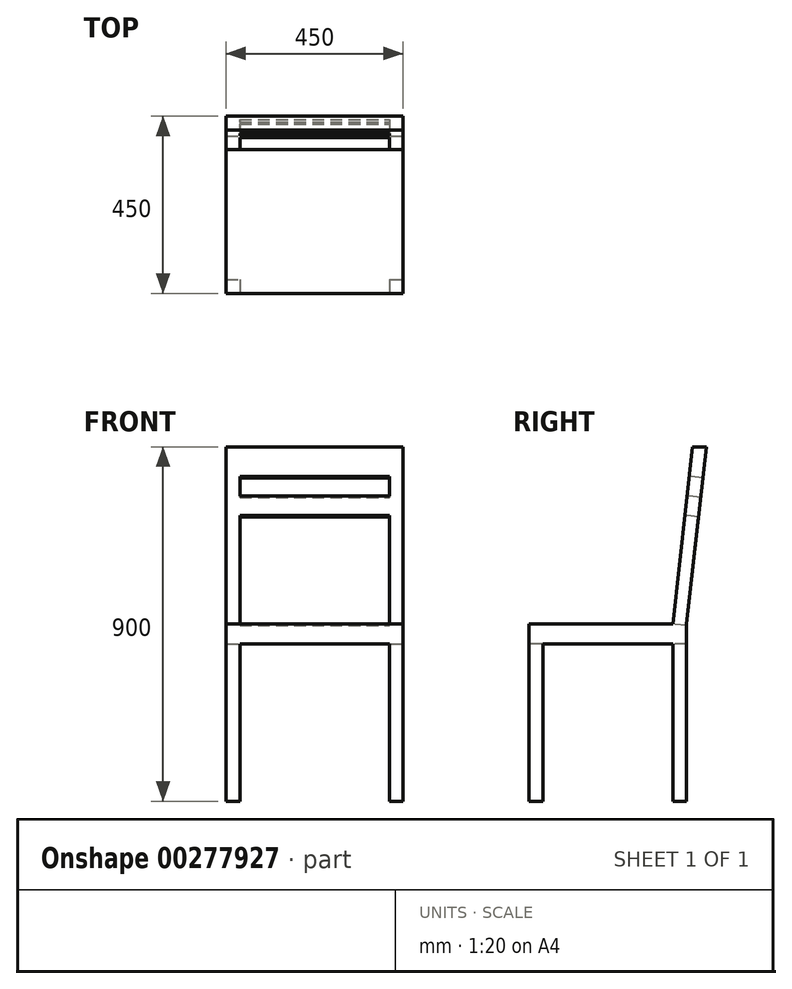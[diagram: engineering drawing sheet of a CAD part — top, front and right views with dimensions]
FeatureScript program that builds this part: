
annotation { "Feature Type Name" : "Feature", "Feature Type Description" : "" }
export const myFeature = defineFeature(function(context is Context, id is Id, definition is map)
    precondition{}
    {
        {
            var Q0;
            Q0=qCreatedBy(makeId("Front.planeOp"),FACE);
            var sketch = newSketch(context, id + "F0", { "sketchPlane" : qUnion([Q0])});
            skLineSegment(sketch, "E0.bottom", {"start": v(-225, 0) * mm, "end": v(225, 0) * mm});
            skLineSegment(sketch, "E0.top", {"start": v(-225, 900) * mm, "end": v(225, 900) * mm});
            skLineSegment(sketch, "E0.left", {"start": v(-225, 0) * mm, "end": v(-225, 900) * mm});
            skLineSegment(sketch, "E0.right", {"start": v(225, 0) * mm, "end": v(225, 900) * mm});
            skSolve(sketch);
        }
        {
            var Q0;
            Q0 = qSketchRegion(id + "F0", true);
            var Q1;
            Q1 = qSketchRegion(id + "F2", true);
            extrude(context, id + "F1", {"entities" : qUnion([Q0, Q1]), "depth" : 450 * mm, "symmetric" : true});
        }
        {
            var Q0;
            Q0=makeQuery(id+"F1.opExtrude","SWEPT_FACE",FACE,{"disambiguationData":[OSD([sQuery(id+"F0.wireOp",EDGE,"E0.right")])]});
            var sketch = newSketch(context, id + "F2", { "sketchPlane" : qUnion([Q0])});
            skLineSegment(sketch, "E1.bottom", {"start": v(225, 450) * mm, "end": v(-225, 450) * mm});
            skLineSegment(sketch, "E1.top", {"start": v(225, 400) * mm, "end": v(-225, 400) * mm});
            skLineSegment(sketch, "E1.left", {"start": v(225, 450) * mm, "end": v(225, 400) * mm});
            skLineSegment(sketch, "E1.right", {"start": v(-225, 450) * mm, "end": v(-225, 400) * mm});
            skLineSegment(sketch, "E2", {"start": v(225, 900) * mm, "end": v(175, 450) * mm});
            skLineSegment(sketch, "E3", {"start": v(190, 900) * mm, "end": v(140, 450) * mm});
            skLineSegment(sketch, "E4", {"start": v(175, 450) * mm, "end": v(175, 0) * mm});
            skLineSegment(sketch, "E5", {"start": v(140, 450) * mm, "end": v(140, 0) * mm});
            skLineSegment(sketch, "E6.bottom", {"start": v(-225, 400) * mm, "end": v(-190, 400) * mm});
            skLineSegment(sketch, "E6.top", {"start": v(-225, 0) * mm, "end": v(-190, 0) * mm});
            skLineSegment(sketch, "E6.left", {"start": v(-225, 400) * mm, "end": v(-225, 0) * mm});
            skLineSegment(sketch, "E6.right", {"start": v(-190, 400) * mm, "end": v(-190, 0) * mm});
            skSolve(sketch);
        }
        {
            var Q0;
            {var subQ4=sQuery(id+"F2.wireOp",EDGE,"E3");Q0=makeQuery(id+"F2.imprint","IMPRINT",FACE,{"disambiguationData":[TD([[makeQuery(id+"F2.imprint","IMPRINT",EDGE,{"derivedFrom":subQ4}),-1.0]])]});}
            var Q1;
            {var subQ4=sQuery(id+"F2.wireOp",EDGE,"E2");Q1=makeQuery(id+"F2.imprint","IMPRINT",FACE,{"disambiguationData":[TD([[makeQuery(id+"F2.imprint","IMPRINT",EDGE,{"derivedFrom":subQ4}),1.0]])]});}
            var Q2;
            {var subQ0=sQuery(id+"F2.wireOp",EDGE,"E1.left");Q2=makeQuery(id+"F2.imprint","IMPRINT",FACE,{"disambiguationData":[TD([[makeQuery(id+"F2.imprint","IMPRINT",EDGE,{"derivedFrom":subQ0}),1.0]])]});}
            var Q3;
            {var subQ0=sQuery(id+"F2.wireOp",EDGE,"E1.top");var subQ4=sQuery(id+"F2.wireOp",EDGE,"E4");var subQ5=makeQuery(id+"F2.imprint","INTERSECT",VERTEX,{"derivedFrom":[subQ0,subQ4]});Q3=makeQuery(id+"F2.imprint","IMPRINT",FACE,{"disambiguationData":[TD([[makeQuery(id+"F2.imprint","IMPRINT",EDGE,{"disambiguationData":[TD([[subQ5,1.0]])],"derivedFrom":subQ0}),1.0]])]});}
            var Q4;
            {var subQ0=sQuery(id+"F2.wireOp",EDGE,"E6.right");Q4=makeQuery(id+"F2.imprint","IMPRINT",FACE,{"disambiguationData":[TD([[makeQuery(id+"F2.imprint","IMPRINT",EDGE,{"derivedFrom":subQ0}),1.0]])]});}
            extrude(context, id + "F3", {"entities" : qUnion([Q0, Q1, Q2, Q3, Q4]), "operationType" : NewBodyOperationType.REMOVE, "endBound" : BoundingType.THROUGH_ALL, "oppositeDirection" : true, "depth" : 25 * mm});
        }
        {
            var Q0;
            Q0=makeQuery(id+"F1.opExtrude","CAP_FACE",FACE,{"disambiguationData":[OSD([sQuery(id+"F0.wireOp",EDGE,"E0.bottom"),sQuery(id+"F0.wireOp",EDGE,"E0.top"),sQuery(id+"F0.wireOp",EDGE,"E0.left"),sQuery(id+"F0.wireOp",EDGE,"E0.right")])],"isStart":false});
            var sketch = newSketch(context, id + "F4", { "sketchPlane" : qUnion([Q0])});
            skLineSegment(sketch, "E7", {"start": v(-190, 0) * mm, "end": v(-190, 400) * mm});
            skLineSegment(sketch, "E8", {"start": v(190, 0) * mm, "end": v(190, 400) * mm});
            skLineSegment(sketch, "E9", {"start": v(-190, 400) * mm, "end": v(190, 400) * mm});
            skSolve(sketch);
        }
        {
            var Q0;
            {var subQ0=sQuery(id+"F4.wireOp",EDGE,"E7");Q0=makeQuery(id+"F4.imprint","IMPRINT",FACE,{"disambiguationData":[TD([[makeQuery(id+"F4.imprint","IMPRINT",EDGE,{"derivedFrom":subQ0}),-1.0]])]});}
            extrude(context, id + "F5", {"entities" : qUnion([Q0]), "operationType" : NewBodyOperationType.REMOVE, "endBound" : BoundingType.THROUGH_ALL, "oppositeDirection" : true, "depth" : 25 * mm});
        }
        {
            var Q0;
            Q0=makeQuery(id+"F3.boolean.opBoolean","COPY",FACE,{"derivedFrom":makeQuery(id+"F3.opExtrude","SWEPT_FACE",FACE,{"disambiguationData":[OSD([sQuery(id+"F2.wireOp",EDGE,"E3")])]})});
            var sketch = newSketch(context, id + "F6", { "sketchPlane" : qUnion([Q0])});
            skLineSegment(sketch, "E10", {"start": v(-190, 462.7) * mm, "end": v(-190, 840.48) * mm});
            skLineSegment(sketch, "E11", {"start": v(-190, 840.48) * mm, "end": v(190, 840.48) * mm});
            skLineSegment(sketch, "E12", {"start": v(190, 840.48) * mm, "end": v(190, 462.7) * mm});
            skLineSegment(sketch, "E13", {"start": v(-190, 790.48) * mm, "end": v(190, 790.48) * mm});
            skLineSegment(sketch, "E14", {"start": v(-190, 740.48) * mm, "end": v(190, 740.48) * mm});
            skSolve(sketch);
        }
        {
            var Q0;
            {var subQ3=sQuery(id+"F6.wireOp",EDGE,"E14");Q0=makeQuery(id+"F6.imprint","IMPRINT",FACE,{"disambiguationData":[TD([[makeQuery(id+"F6.imprint","IMPRINT",EDGE,{"derivedFrom":subQ3}),-1.0]])]});}
            var Q1;
            {var subQ0=sQuery(id+"F6.wireOp",EDGE,"E11");Q1=makeQuery(id+"F6.imprint","IMPRINT",FACE,{"disambiguationData":[TD([[makeQuery(id+"F6.imprint","IMPRINT",EDGE,{"derivedFrom":subQ0}),-1.0]])]});}
            extrude(context, id + "F7", {"entities" : qUnion([Q0, Q1]), "operationType" : NewBodyOperationType.REMOVE, "endBound" : BoundingType.THROUGH_ALL, "oppositeDirection" : true, "depth" : 25 * mm});
        }
    });
